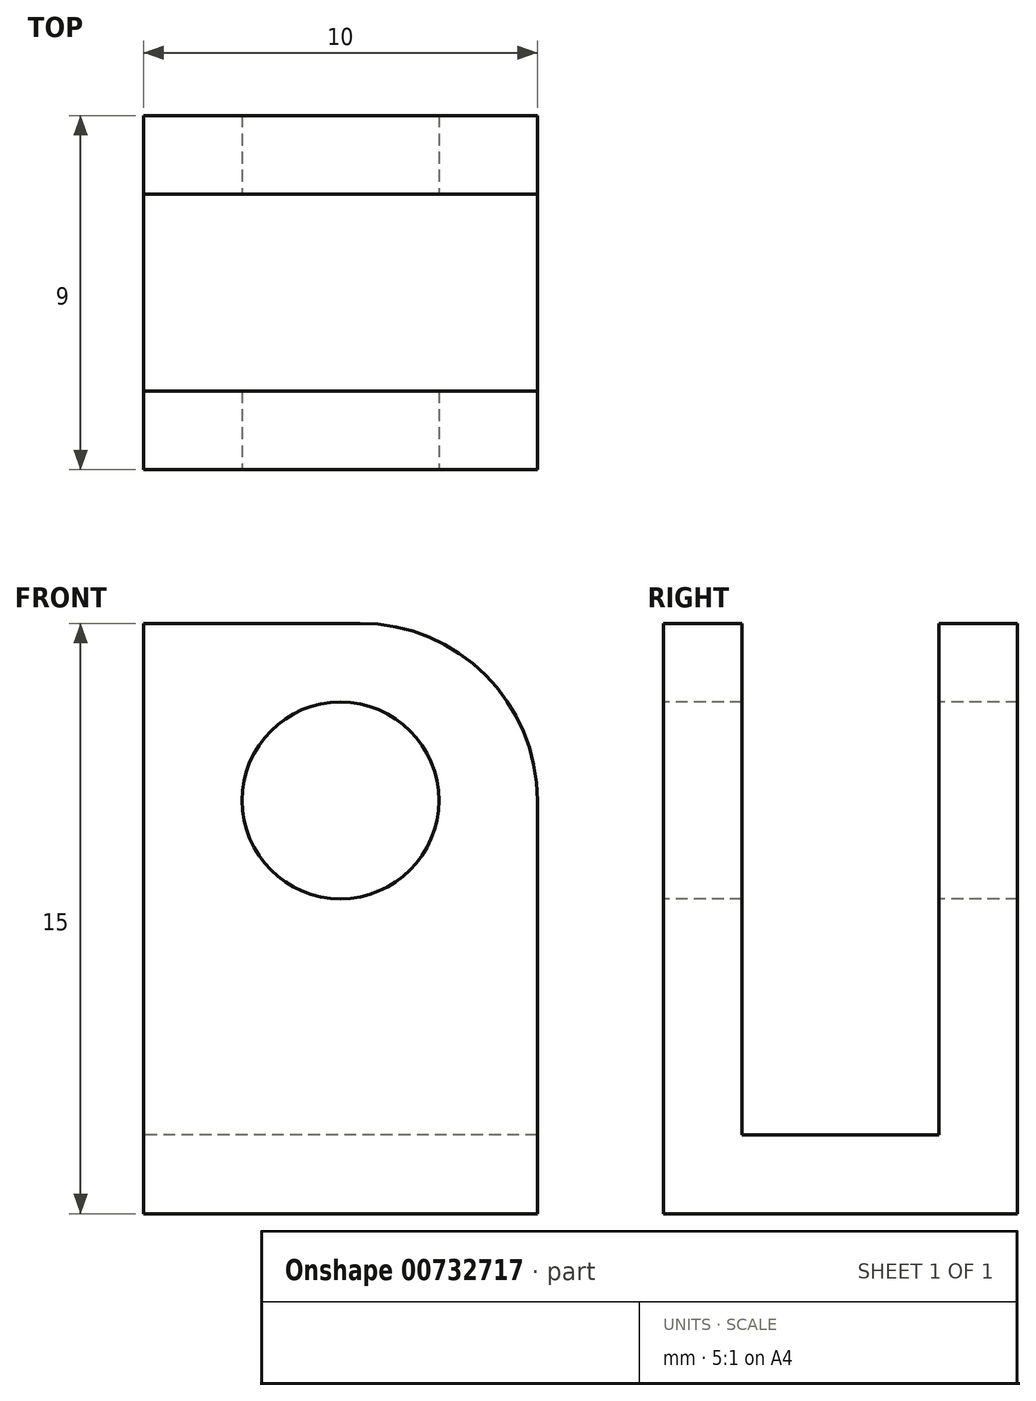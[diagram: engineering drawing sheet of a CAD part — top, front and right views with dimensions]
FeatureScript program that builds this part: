
annotation { "Feature Type Name" : "Feature", "Feature Type Description" : "" }
export const myFeature = defineFeature(function(context is Context, id is Id, definition is map)
    precondition{}
    {
        {
            assignVariable(context, id + "F0", {"name" : "t", "anyValue" : 2 * mm});
        }
        {
            assignVariable(context, id + "F1", {"name" : "id", "anyValue" : 5 * mm});
        }
        {
            assignVariable(context, id + "F2", {"name" : "sw", "anyValue" : 5 * mm});
        }
        {
            assignVariable(context, id + "F3", {"name" : "d", "anyValue" : getVariable(context, 'sw') + getVariable(context, 't') * 2});
        }
        {
            var Q0;
            Q0=qCreatedBy(makeId("Front.planeOp"),FACE);
            var sketch = newSketch(context, id + "F4", { "sketchPlane" : qUnion([Q0])});
            skLineSegment(sketch, "E0.bottom", {"start": v(-5, 0) * mm, "end": v(5, 0) * mm});
            skLineSegment(sketch, "E0.top", {"start": v(-5, 15) * mm, "end": v(5, 15) * mm});
            skLineSegment(sketch, "E0.left", {"start": v(-5, 0) * mm, "end": v(-5, 15) * mm});
            skLineSegment(sketch, "E0.right", {"start": v(5, 0) * mm, "end": v(5, 15) * mm});
            skSolve(sketch);
        }
        {
            var Q0;
            Q0=makeQuery(id+"F4.imprint","IMPRINT",FACE,{"disambiguationData":[TD([[makeQuery(id+"F4.imprint","IMPRINT",EDGE,{"derivedFrom":sQuery(id+"F4.wireOp",EDGE,"E0.bottom")}),1.0]])]});
            extrude(context, id + "F5", {"entities" : qUnion([Q0]), "depth" : getVariable(context, 'd'), "offsetDistance" : 25 * mm});
        }
        {
            var Q0;
            Q0=makeQuery(id+"F5.opExtrude","CAP_FACE",FACE,{"disambiguationData":[OSD([sQuery(id+"F4.wireOp",EDGE,"E0.bottom"),sQuery(id+"F4.wireOp",EDGE,"E0.top"),sQuery(id+"F4.wireOp",EDGE,"E0.left"),sQuery(id+"F4.wireOp",EDGE,"E0.right")])],"isStart":false});
            var sketch = newSketch(context, id + "F6", { "sketchPlane" : qUnion([Q0])});
            skCircle(sketch, "E1", {"center": v(0, 10.5) * mm, "radius": 2.5 * mm});
            skSolve(sketch);
        }
        {
            var Q0;
            Q0=makeQuery(id+"F6.imprint","IMPRINT",FACE,{"disambiguationData":[TD([[makeQuery(id+"F6.imprint","IMPRINT",EDGE,{"derivedFrom":sQuery(id+"F6.wireOp",EDGE,"E1")}),1.0]])]});
            extrude(context, id + "F7", {"entities" : qUnion([Q0]), "operationType" : NewBodyOperationType.REMOVE, "endBound" : BoundingType.THROUGH_ALL, "oppositeDirection" : true, "depth" : 25 * mm, "offsetDistance" : 25 * mm});
        }
        {
            var Q0;
            Q0=makeQuery(id+"F5.opExtrude","SWEPT_EDGE",EDGE,{"disambiguationData":[OSD([sQuery(id+"F4.wireOp",EDGE,"E0.top"),sQuery(id+"F4.wireOp",EDGE,"E0.right")])]});
            fillet(context, id + "F8", {"entities" : qUnion([Q0]), "radius" : getVariable(context, 't') + getVariable(context, 'id') / 2, "tangentPropagation" : true, "allowEdgeOverflow" : false});
        }
        {
            var Q0;
            Q0=makeQuery(id+"F5.opExtrude","SWEPT_FACE",FACE,{"disambiguationData":[OSD([sQuery(id+"F4.wireOp",EDGE,"E0.left")])]});
            var sketch = newSketch(context, id + "F9", { "sketchPlane" : qUnion([Q0])});
            skLineSegment(sketch, "E2.bottom", {"start": v(2, 15) * mm, "end": v(7, 15) * mm});
            skLineSegment(sketch, "E2.top", {"start": v(2, 2) * mm, "end": v(7, 2) * mm});
            skLineSegment(sketch, "E2.left", {"start": v(2, 15) * mm, "end": v(2, 2) * mm});
            skLineSegment(sketch, "E2.right", {"start": v(7, 15) * mm, "end": v(7, 2) * mm});
            skSolve(sketch);
        }
        {
            var Q0;
            Q0=makeQuery(id+"F9.imprint","IMPRINT",FACE,{"disambiguationData":[TD([[makeQuery(id+"F9.imprint","IMPRINT",EDGE,{"derivedFrom":sQuery(id+"F9.wireOp",EDGE,"E2.bottom")}),1.0]])]});
            extrude(context, id + "F10", {"entities" : qUnion([Q0]), "operationType" : NewBodyOperationType.REMOVE, "endBound" : BoundingType.THROUGH_ALL, "oppositeDirection" : true, "depth" : 25 * mm, "offsetDistance" : 25 * mm});
        }
    });
